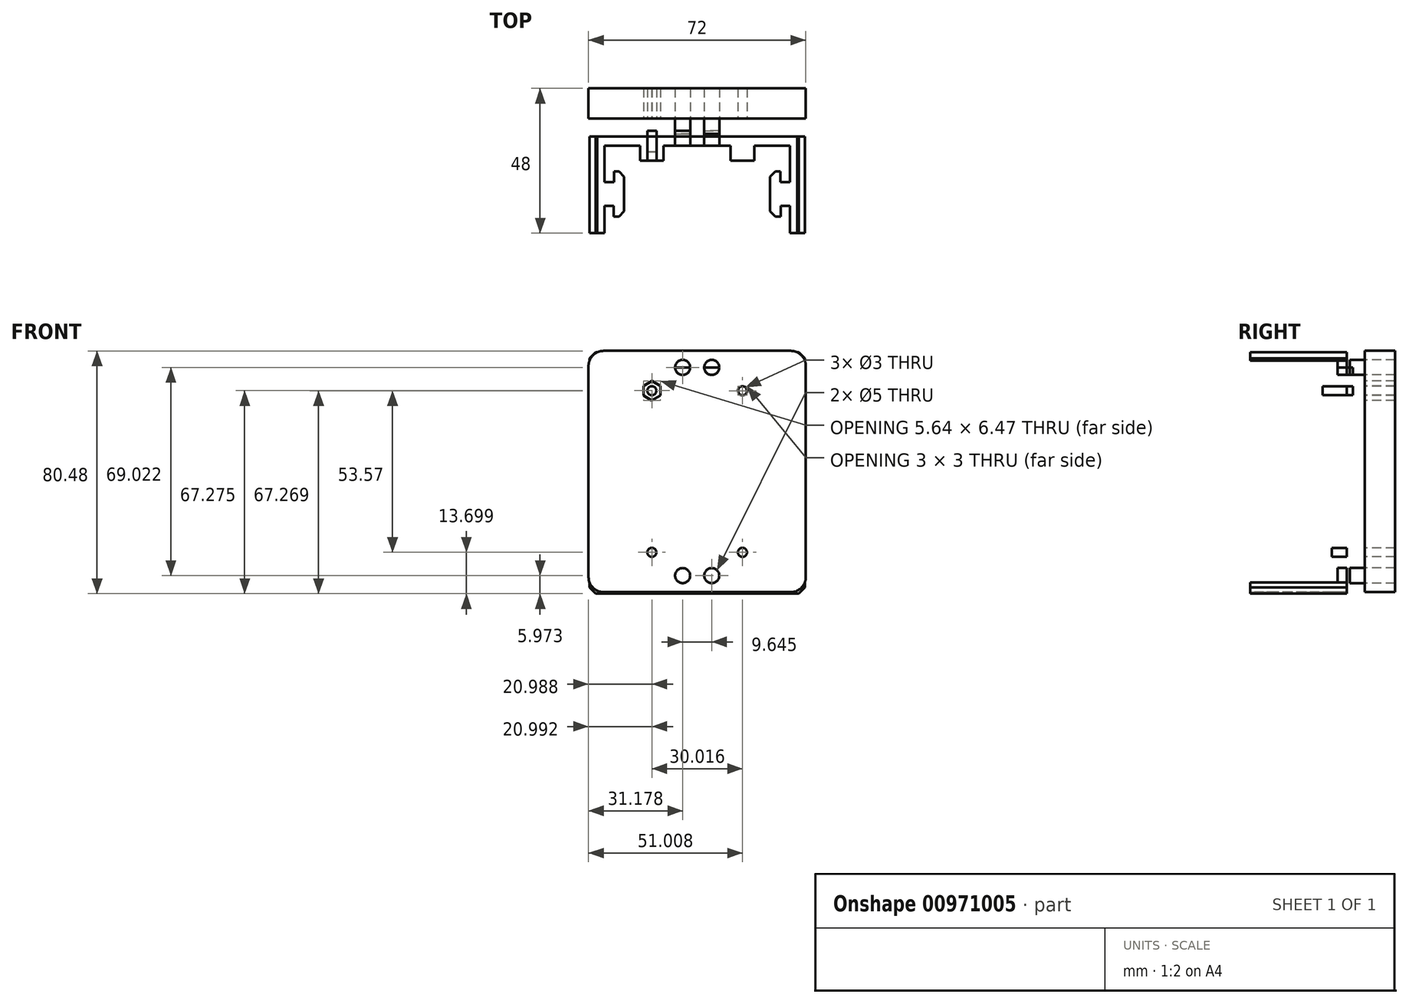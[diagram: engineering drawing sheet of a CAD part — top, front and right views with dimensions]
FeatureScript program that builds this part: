
annotation { "Feature Type Name" : "Feature", "Feature Type Description" : "" }
export const myFeature = defineFeature(function(context is Context, id is Id, definition is map)
    precondition{}
    {
        {
            var Q0;
            Q0=qCreatedBy(makeId("Top.planeOp"),FACE);
            var sketch = newSketch(context, id + "F0", { "sketchPlane" : qUnion([Q0])});
            skLineSegment(sketch, "E0.bottom", {"start": v(30, -15) * mm, "end": v(-30, -15) * mm});
            skLineSegment(sketch, "E0.top", {"start": v(30, 15) * mm, "end": v(-30, 15) * mm});
            skLineSegment(sketch, "E0.left", {"start": v(30, -15) * mm, "end": v(30, 15) * mm});
            skLineSegment(sketch, "E0.right", {"start": v(-30, -15) * mm, "end": v(-30, 15) * mm});
            skPoint(sketch, "E0.middle", {"position": v(0, 0) * mm});
            skLineSegment(sketch, "E1", {"start": v(0, 15) * mm, "end": v(0, -15) * mm});
            skLineSegment(sketch, "E2", {"start": v(35.69, 0) * mm, "end": v(35.69, 13) * mm});
            skLineSegment(sketch, "E3", {"start": v(35.69, 13) * mm, "end": v(35.69, 0) * mm});
            skLineSegment(sketch, "E4", {"start": v(35.69, -13) * mm, "end": v(35.69, 0) * mm});
            skLineSegment(sketch, "E5", {"start": v(35.69, 13) * mm, "end": v(30.75, 13) * mm});
            skLineSegment(sketch, "E6", {"start": v(30.75, 13) * mm, "end": v(30.75, -13) * mm});
            skLineSegment(sketch, "E7", {"start": v(30.75, -13) * mm, "end": v(35.69, -13) * mm});
            skLineSegment(sketch, "E8", {"start": v(35.69, 0) * mm, "end": v(24.19, 0) * mm});
            skLineSegment(sketch, "E9", {"start": v(24.19, 0) * mm, "end": v(24.19, -7.5) * mm});
            skLineSegment(sketch, "E10", {"start": v(24.19, -7.5) * mm, "end": v(24.19, 7.5) * mm});
            skLineSegment(sketch, "E11", {"start": v(24.19, 7.5) * mm, "end": v(27.59, 7.5) * mm});
            skLineSegment(sketch, "E12", {"start": v(27.59, 7.5) * mm, "end": v(27.59, 3.9) * mm});
            skLineSegment(sketch, "E13", {"start": v(27.59, 3.9) * mm, "end": v(30.75, 3.9) * mm});
            skLineSegment(sketch, "E14", {"start": v(30.75, 3.9) * mm, "end": v(30.75, -3.9) * mm});
            skLineSegment(sketch, "E15", {"start": v(30.75, -3.9) * mm, "end": v(27.65, -3.9) * mm});
            skLineSegment(sketch, "E16", {"start": v(27.65, -3.9) * mm, "end": v(27.65, -7.5) * mm});
            skLineSegment(sketch, "E17", {"start": v(27.65, -7.5) * mm, "end": v(24.19, -7.5) * mm});
            skLineSegment(sketch, "E18", {"start": v(25.89, 7.5) * mm, "end": v(24.19, 5.67) * mm});
            skLineSegment(sketch, "E19.MirrorCS", {"start": v(25.89, -7.5) * mm, "end": v(24.19, -5.67) * mm});
            skPoint(sketch, "E20.middle", {"position": v(33.19, 0) * mm});
            skLineSegment(sketch, "E21.bottom", {"start": v(30.75, 13) * mm, "end": v(35.69, 13) * mm});
            skLineSegment(sketch, "E21.left", {"start": v(30.75, 13) * mm, "end": v(30.75, 16) * mm});
            skLineSegment(sketch, "E21.right", {"start": v(35.69, 13) * mm, "end": v(35.69, 19) * mm});
            skLineSegment(sketch, "E22", {"start": v(15, 15) * mm, "end": v(15, -15) * mm, "construction": true});
            skLineSegment(sketch, "E23.bottom", {"start": v(18.9, 11) * mm, "end": v(11.1, 11) * mm});
            skLineSegment(sketch, "E23.top", {"start": v(18.9, 19) * mm, "end": v(11.1, 19) * mm});
            skLineSegment(sketch, "E23.left", {"start": v(18.9, 11) * mm, "end": v(18.9, 19) * mm});
            skLineSegment(sketch, "E23.right", {"start": v(11.1, 11) * mm, "end": v(11.1, 19) * mm});
            skPoint(sketch, "E23.middle", {"position": v(15, 15) * mm});
            skLineSegment(sketch, "E24", {"start": v(18.9, 19) * mm, "end": v(35.69, 19) * mm});
            skLineSegment(sketch, "E25", {"start": v(35.69, 19) * mm, "end": v(35.69, 19) * mm});
            skLineSegment(sketch, "E26", {"start": v(18.9, 16) * mm, "end": v(30.75, 16) * mm});
            skLineSegment(sketch, "E27", {"start": v(11.1, 19) * mm, "end": v(0, 19) * mm});
            skLineSegment(sketch, "E28", {"start": v(11.1, 16) * mm, "end": v(0, 16) * mm});
            skLineSegment(sketch, "E29", {"start": v(0, 16) * mm, "end": v(0, 19) * mm});
            skLineSegment(sketch, "E30.MirrorCS", {"start": v(-11.1, 16) * mm, "end": v(0, 16) * mm});
            skLineSegment(sketch, "E31.MirrorCS", {"start": v(-11.1, 11) * mm, "end": v(-11.1, 19) * mm});
            skLineSegment(sketch, "E32.MirrorCS", {"start": v(-18.9, 11) * mm, "end": v(-11.1, 11) * mm});
            skLineSegment(sketch, "E33.MirrorCS", {"start": v(-18.9, 11) * mm, "end": v(-18.9, 19) * mm});
            skLineSegment(sketch, "E34.MirrorCS", {"start": v(-18.9, 16) * mm, "end": v(-30.75, 16) * mm});
            skLineSegment(sketch, "E35.MirrorCS", {"start": v(-30.75, 13) * mm, "end": v(-30.75, 16) * mm});
            skLineSegment(sketch, "E36.MirrorCS", {"start": v(-35.69, 13) * mm, "end": v(-35.69, 19) * mm});
            skLineSegment(sketch, "E37.MirrorCS", {"start": v(-35.69, 19) * mm, "end": v(-35.69, 19) * mm});
            skLineSegment(sketch, "E38.MirrorCS", {"start": v(-18.9, 19) * mm, "end": v(-35.69, 19) * mm});
            skLineSegment(sketch, "E39.MirrorCS", {"start": v(-11.1, 19) * mm, "end": v(0, 19) * mm});
            skLineSegment(sketch, "E40.MirrorCS", {"start": v(-18.9, 19) * mm, "end": v(-11.1, 19) * mm});
            skLineSegment(sketch, "E41.MirrorCS", {"start": v(-30.75, 13) * mm, "end": v(-30.75, -13) * mm});
            skLineSegment(sketch, "E42.MirrorCS", {"start": v(-35.69, 13) * mm, "end": v(-35.69, 0) * mm});
            skLineSegment(sketch, "E43.MirrorCS", {"start": v(-30.75, -13) * mm, "end": v(-35.69, -13) * mm});
            skLineSegment(sketch, "E44.MirrorCS", {"start": v(-35.69, -13) * mm, "end": v(-35.69, 0) * mm});
            skLineSegment(sketch, "E45.MirrorCS", {"start": v(-30.75, -3.9) * mm, "end": v(-27.65, -3.9) * mm});
            skLineSegment(sketch, "E46.MirrorCS", {"start": v(-27.59, 3.9) * mm, "end": v(-30.75, 3.9) * mm});
            skLineSegment(sketch, "E47.MirrorCS", {"start": v(-24.19, -7.5) * mm, "end": v(-24.19, 7.5) * mm});
            skLineSegment(sketch, "E48.MirrorCS", {"start": v(-25.89, 7.5) * mm, "end": v(-24.19, 5.67) * mm});
            skLineSegment(sketch, "E49.MirrorCS", {"start": v(-24.19, 7.5) * mm, "end": v(-27.59, 7.5) * mm});
            skLineSegment(sketch, "E50.MirrorCS", {"start": v(-27.59, 7.5) * mm, "end": v(-27.59, 3.9) * mm});
            skLineSegment(sketch, "E51.MirrorCS", {"start": v(-27.65, -3.9) * mm, "end": v(-27.65, -7.5) * mm});
            skLineSegment(sketch, "E52.MirrorCS", {"start": v(-27.65, -7.5) * mm, "end": v(-24.19, -7.5) * mm});
            skLineSegment(sketch, "E53.MirrorCS", {"start": v(-25.89, -7.5) * mm, "end": v(-24.19, -5.67) * mm});
            skLineSegment(sketch, "E54.bottom", {"start": v(-35.69, 19) * mm, "end": v(35.69, 19) * mm});
            skLineSegment(sketch, "E54.top", {"start": v(-35.69, 21) * mm, "end": v(35.69, 21) * mm});
            skLineSegment(sketch, "E54.left", {"start": v(-35.69, 19) * mm, "end": v(-35.69, 21) * mm});
            skLineSegment(sketch, "E54.right", {"start": v(35.69, 19) * mm, "end": v(35.69, 21) * mm});
            skSolve(sketch);
        }
        {
            var Q0;
            {var subQ5=sQuery(id+"F0.wireOp",EDGE,"E4");Q0=makeQuery(id+"F0.imprint","IMPRINT",FACE,{"disambiguationData":[TD([[makeQuery(id+"F0.imprint","IMPRINT",EDGE,{"derivedFrom":subQ5}),1.0]])]});}
            var Q1;
            {var subQ3=sQuery(id+"F0.wireOp",EDGE,"E16");Q1=makeQuery(id+"F0.imprint","IMPRINT",FACE,{"disambiguationData":[TD([[makeQuery(id+"F0.imprint","IMPRINT",EDGE,{"derivedFrom":subQ3}),-1.0]])]});}
            var Q2;
            {var subQ0=sQuery(id+"F0.wireOp",EDGE,"E8");var subQ1=sQuery(id+"F0.wireOp",EDGE,"E0.left");var subQ2=makeQuery(id+"F0.imprint","INTERSECT",VERTEX,{"derivedFrom":[subQ1,subQ0]});Q2=makeQuery(id+"F0.imprint","IMPRINT",FACE,{"disambiguationData":[TD([[makeQuery(id+"F0.imprint","IMPRINT",EDGE,{"disambiguationData":[TD([[subQ2,1.0]])],"derivedFrom":subQ1}),-1.0]])]});}
            var Q3;
            {var subQ0=sQuery(id+"F0.wireOp",EDGE,"E13");var subQ1=sQuery(id+"F0.wireOp",EDGE,"E0.left");var subQ2=makeQuery(id+"F0.imprint","INTERSECT",VERTEX,{"derivedFrom":[subQ1,subQ0]});Q3=makeQuery(id+"F0.imprint","IMPRINT",FACE,{"disambiguationData":[TD([[makeQuery(id+"F0.imprint","IMPRINT",EDGE,{"disambiguationData":[TD([[subQ2,1.0]])],"derivedFrom":subQ1}),-1.0]])]});}
            var Q4;
            {var subQ7=sQuery(id+"F0.wireOp",EDGE,"E12");Q4=makeQuery(id+"F0.imprint","IMPRINT",FACE,{"disambiguationData":[TD([[makeQuery(id+"F0.imprint","IMPRINT",EDGE,{"derivedFrom":subQ7}),-1.0]])]});}
            var Q5;
            {var subQ5=sQuery(id+"F0.wireOp",EDGE,"E2");Q5=makeQuery(id+"F0.imprint","IMPRINT",FACE,{"disambiguationData":[TD([[makeQuery(id+"F0.imprint","IMPRINT",EDGE,{"derivedFrom":subQ5}),1.0]])]});}
            var Q6;
            Q6=makeQuery(id+"F0.imprint","IMPRINT",FACE,{"disambiguationData":[TD([[makeQuery(id+"F0.imprint","IMPRINT",EDGE,{"derivedFrom":sQuery(id+"F0.wireOp",EDGE,"E5")}),-1.0]])]});
            var Q7;
            {var subQ1=sQuery(id+"F0.wireOp",EDGE,"E23.top");Q7=makeQuery(id+"F0.imprint","IMPRINT",FACE,{"disambiguationData":[TD([[makeQuery(id+"F0.imprint","IMPRINT",EDGE,{"derivedFrom":subQ1}),1.0]])]});}
            var Q8;
            {var subQ0=sQuery(id+"F0.wireOp",EDGE,"E27");Q8=makeQuery(id+"F0.imprint","IMPRINT",FACE,{"disambiguationData":[TD([[makeQuery(id+"F0.imprint","IMPRINT",EDGE,{"derivedFrom":subQ0}),1.0]])]});}
            var Q9;
            Q9=makeQuery(id+"F0.imprint","IMPRINT",FACE,{"disambiguationData":[TD([[makeQuery(id+"F0.imprint","IMPRINT",EDGE,{"derivedFrom":sQuery(id+"F0.wireOp",EDGE,"E29")}),1.0]])]});
            var Q10;
            {var subQ6=sQuery(id+"F0.wireOp",EDGE,"E40.MirrorCS");Q10=makeQuery(id+"F0.imprint","IMPRINT",FACE,{"disambiguationData":[TD([[makeQuery(id+"F0.imprint","IMPRINT",EDGE,{"derivedFrom":subQ6}),-1.0]])]});}
            var Q11;
            {var subQ6=sQuery(id+"F0.wireOp",EDGE,"E34.MirrorCS");Q11=makeQuery(id+"F0.imprint","IMPRINT",FACE,{"disambiguationData":[TD([[makeQuery(id+"F0.imprint","IMPRINT",EDGE,{"derivedFrom":subQ6}),-1.0]])]});}
            var Q12;
            {var subQ5=sQuery(id+"F0.wireOp",EDGE,"E32.MirrorCS");Q12=makeQuery(id+"F0.imprint","IMPRINT",FACE,{"disambiguationData":[TD([[makeQuery(id+"F0.imprint","IMPRINT",EDGE,{"derivedFrom":subQ5}),1.0]])]});}
            var Q13;
            {var subQ5=sQuery(id+"F0.wireOp",EDGE,"E23.bottom");Q13=makeQuery(id+"F0.imprint","IMPRINT",FACE,{"disambiguationData":[TD([[makeQuery(id+"F0.imprint","IMPRINT",EDGE,{"derivedFrom":subQ5}),-1.0]])]});}
            var Q14;
            {var subQ2=sQuery(id+"F0.wireOp",EDGE,"E48.MirrorCS");Q14=makeQuery(id+"F0.imprint","IMPRINT",FACE,{"disambiguationData":[TD([[makeQuery(id+"F0.imprint","IMPRINT",EDGE,{"derivedFrom":subQ2}),-1.0]])]});}
            var Q15;
            {var subQ0=sQuery(id+"F0.wireOp",EDGE,"E46.MirrorCS");var subQ1=sQuery(id+"F0.wireOp",EDGE,"E0.right");var subQ2=makeQuery(id+"F0.imprint","INTERSECT",VERTEX,{"derivedFrom":[subQ1,subQ0]});Q15=makeQuery(id+"F0.imprint","IMPRINT",FACE,{"disambiguationData":[TD([[makeQuery(id+"F0.imprint","IMPRINT",EDGE,{"disambiguationData":[TD([[subQ2,1.0]])],"derivedFrom":subQ1}),1.0]])]});}
            var Q16;
            {var subQ2=sQuery(id+"F0.wireOp",EDGE,"E40.MirrorCS");Q16=makeQuery(id+"F0.imprint","IMPRINT",FACE,{"disambiguationData":[TD([[makeQuery(id+"F0.imprint","IMPRINT",EDGE,{"derivedFrom":subQ2}),-1.0]])]});}
            var Q17;
            Q17=makeQuery(id+"F0.imprint","IMPRINT",FACE,{"disambiguationData":[TD([[makeQuery(id+"F0.imprint","IMPRINT",EDGE,{"derivedFrom":sQuery(id+"F0.wireOp",EDGE,"E23.top")}),-1.0]])]});
            var Q18;
            {var subQ4=sQuery(id+"F0.wireOp",EDGE,"E23.top");Q18=makeQuery(id+"F0.imprint","IMPRINT",FACE,{"disambiguationData":[TD([[makeQuery(id+"F0.imprint","IMPRINT",EDGE,{"derivedFrom":subQ4}),1.0]])]});}
            var Q19;
            {var subQ0=sQuery(id+"F0.wireOp",EDGE,"E27");Q19=makeQuery(id+"F0.imprint","IMPRINT",FACE,{"disambiguationData":[TD([[makeQuery(id+"F0.imprint","IMPRINT",EDGE,{"derivedFrom":subQ0}),1.0]])]});}
            extrude(context, id + "F1", {"entities" : qUnion([Q0, Q1, Q2, Q3, Q4, Q5, Q6, Q7, Q8, Q9, Q10, Q11, Q12, Q13, Q14, Q15, Q16, Q17, Q18, Q19]), "oppositeDirection" : true, "depth" : 20 * mm, "offsetDistance" : 25 * mm});
        }
        {
            var Q0;
            Q0=makeQuery(id+"F1.opExtrude","SWEPT_FACE",FACE,{"disambiguationData":[OSD([sQuery(id+"F0.wireOp",EDGE,"E32.MirrorCS")])]});
            var Q1;
            Q1=makeQuery(id+"F1.opExtrude","SWEPT_FACE",FACE,{"disambiguationData":[OSD([sQuery(id+"F0.wireOp",EDGE,"E23.bottom")])]});
            var Q2;
            Q2=makeQuery(id+"F1.opExtrude","SWEPT_EDGE",EDGE,{"disambiguationData":[OSD([sQuery(id+"F0.wireOp",EDGE,"E43.MirrorCS"),sQuery(id+"F0.wireOp",EDGE,"E44.MirrorCS")])]});
            var Q3;
            Q3=makeQuery(id+"F1.opExtrude","SWEPT_EDGE",EDGE,{"disambiguationData":[OSD([sQuery(id+"F0.wireOp",EDGE,"E41.MirrorCS"),sQuery(id+"F0.wireOp",EDGE,"E43.MirrorCS")])]});
            var Q4;
            Q4=makeQuery(id+"F1.opExtrude","SWEPT_EDGE",EDGE,{"disambiguationData":[OSD([sQuery(id+"F0.wireOp",EDGE,"E6"),sQuery(id+"F0.wireOp",EDGE,"E7")])]});
            var Q5;
            Q5=makeQuery(id+"F1.opExtrude","SWEPT_EDGE",EDGE,{"disambiguationData":[OSD([sQuery(id+"F0.wireOp",EDGE,"E4"),sQuery(id+"F0.wireOp",EDGE,"E7")])]});
            var Q6;
            Q6=makeQuery(id+"F1.opExtrude","SWEPT_EDGE",EDGE,{"disambiguationData":[OSD([sQuery(id+"F0.wireOp",EDGE,"E24"),sQuery(id+"F0.wireOp",EDGE,"E25")])]});
            var Q7;
            Q7=makeQuery(id+"F1.opExtrude","SWEPT_EDGE",EDGE,{"disambiguationData":[OSD([sQuery(id+"F0.wireOp",EDGE,"E37.MirrorCS"),sQuery(id+"F0.wireOp",EDGE,"E38.MirrorCS")])]});
            chamfer(context, id + "F2", {"entities" : qUnion([Q0, Q1, Q2, Q3, Q4, Q5, Q6, Q7]), "width" : 1.2 * mm, "tangentPropagation" : true});
        }
        {
            var Q0;
            {var subQ6=sQuery(id+"F0.wireOp",EDGE,"E34.MirrorCS");Q0=makeQuery(id+"F0.imprint","IMPRINT",FACE,{"disambiguationData":[TD([[makeQuery(id+"F0.imprint","IMPRINT",EDGE,{"derivedFrom":subQ6}),-1.0]])]});}
            var Q1;
            {var subQ0=sQuery(id+"F0.wireOp",EDGE,"E46.MirrorCS");var subQ1=sQuery(id+"F0.wireOp",EDGE,"E0.right");var subQ2=makeQuery(id+"F0.imprint","INTERSECT",VERTEX,{"derivedFrom":[subQ1,subQ0]});Q1=makeQuery(id+"F0.imprint","IMPRINT",FACE,{"disambiguationData":[TD([[makeQuery(id+"F0.imprint","IMPRINT",EDGE,{"disambiguationData":[TD([[subQ2,1.0]])],"derivedFrom":subQ1}),1.0]])]});}
            var Q2;
            {var subQ2=sQuery(id+"F0.wireOp",EDGE,"E48.MirrorCS");Q2=makeQuery(id+"F0.imprint","IMPRINT",FACE,{"disambiguationData":[TD([[makeQuery(id+"F0.imprint","IMPRINT",EDGE,{"derivedFrom":subQ2}),-1.0]])]});}
            var Q3;
            {var subQ2=sQuery(id+"F0.wireOp",EDGE,"E40.MirrorCS");Q3=makeQuery(id+"F0.imprint","IMPRINT",FACE,{"disambiguationData":[TD([[makeQuery(id+"F0.imprint","IMPRINT",EDGE,{"derivedFrom":subQ2}),-1.0]])]});}
            var Q4;
            Q4=makeQuery(id+"F0.imprint","IMPRINT",FACE,{"disambiguationData":[TD([[makeQuery(id+"F0.imprint","IMPRINT",EDGE,{"derivedFrom":sQuery(id+"F0.wireOp",EDGE,"E29")}),1.0]])]});
            var Q5;
            {var subQ0=sQuery(id+"F0.wireOp",EDGE,"E27");Q5=makeQuery(id+"F0.imprint","IMPRINT",FACE,{"disambiguationData":[TD([[makeQuery(id+"F0.imprint","IMPRINT",EDGE,{"derivedFrom":subQ0}),1.0]])]});}
            var Q6;
            {var subQ4=sQuery(id+"F0.wireOp",EDGE,"E23.top");Q6=makeQuery(id+"F0.imprint","IMPRINT",FACE,{"disambiguationData":[TD([[makeQuery(id+"F0.imprint","IMPRINT",EDGE,{"derivedFrom":subQ4}),1.0]])]});}
            var Q7;
            Q7=makeQuery(id+"F0.imprint","IMPRINT",FACE,{"disambiguationData":[TD([[makeQuery(id+"F0.imprint","IMPRINT",EDGE,{"derivedFrom":sQuery(id+"F0.wireOp",EDGE,"E5")}),-1.0]])]});
            var Q8;
            {var subQ5=sQuery(id+"F0.wireOp",EDGE,"E2");Q8=makeQuery(id+"F0.imprint","IMPRINT",FACE,{"disambiguationData":[TD([[makeQuery(id+"F0.imprint","IMPRINT",EDGE,{"derivedFrom":subQ5}),1.0]])]});}
            var Q9;
            {var subQ5=sQuery(id+"F0.wireOp",EDGE,"E4");Q9=makeQuery(id+"F0.imprint","IMPRINT",FACE,{"disambiguationData":[TD([[makeQuery(id+"F0.imprint","IMPRINT",EDGE,{"derivedFrom":subQ5}),1.0]])]});}
            var Q10;
            {var subQ3=sQuery(id+"F0.wireOp",EDGE,"E16");Q10=makeQuery(id+"F0.imprint","IMPRINT",FACE,{"disambiguationData":[TD([[makeQuery(id+"F0.imprint","IMPRINT",EDGE,{"derivedFrom":subQ3}),-1.0]])]});}
            var Q11;
            Q11=makeQuery(id+"F0.imprint","IMPRINT",FACE,{"disambiguationData":[TD([[makeQuery(id+"F0.imprint","IMPRINT",EDGE,{"derivedFrom":sQuery(id+"F0.wireOp",EDGE,"E23.top")}),-1.0]])]});
            var Q12;
            {var subQ5=sQuery(id+"F0.wireOp",EDGE,"E32.MirrorCS");Q12=makeQuery(id+"F0.imprint","IMPRINT",FACE,{"disambiguationData":[TD([[makeQuery(id+"F0.imprint","IMPRINT",EDGE,{"derivedFrom":subQ5}),1.0]])]});}
            var Q13;
            {var subQ5=sQuery(id+"F0.wireOp",EDGE,"E23.bottom");Q13=makeQuery(id+"F0.imprint","IMPRINT",FACE,{"disambiguationData":[TD([[makeQuery(id+"F0.imprint","IMPRINT",EDGE,{"derivedFrom":subQ5}),-1.0]])]});}
            var Q14;
            {var subQ7=sQuery(id+"F0.wireOp",EDGE,"E12");Q14=makeQuery(id+"F0.imprint","IMPRINT",FACE,{"disambiguationData":[TD([[makeQuery(id+"F0.imprint","IMPRINT",EDGE,{"derivedFrom":subQ7}),-1.0]])]});}
            var Q15;
            {var subQ0=sQuery(id+"F0.wireOp",EDGE,"E8");var subQ1=sQuery(id+"F0.wireOp",EDGE,"E0.left");var subQ2=makeQuery(id+"F0.imprint","INTERSECT",VERTEX,{"derivedFrom":[subQ1,subQ0]});Q15=makeQuery(id+"F0.imprint","IMPRINT",FACE,{"disambiguationData":[TD([[makeQuery(id+"F0.imprint","IMPRINT",EDGE,{"disambiguationData":[TD([[subQ2,1.0]])],"derivedFrom":subQ1}),-1.0]])]});}
            var Q16;
            {var subQ0=sQuery(id+"F0.wireOp",EDGE,"E13");var subQ1=sQuery(id+"F0.wireOp",EDGE,"E0.left");var subQ2=makeQuery(id+"F0.imprint","INTERSECT",VERTEX,{"derivedFrom":[subQ1,subQ0]});Q16=makeQuery(id+"F0.imprint","IMPRINT",FACE,{"disambiguationData":[TD([[makeQuery(id+"F0.imprint","IMPRINT",EDGE,{"disambiguationData":[TD([[subQ2,1.0]])],"derivedFrom":subQ1}),-1.0]])]});}
            extrude(context, id + "F3", {"entities" : qUnion([Q0, Q1, Q2, Q3, Q4, Q5, Q6, Q7, Q8, Q9, Q10, Q11, Q12, Q13, Q14, Q15, Q16]), "depth" : 15 * mm, "offsetDistance" : 25 * mm});
        }
        {
            var Q0;
            Q0=makeQuery(id+"F3.opExtrude","SWEPT_EDGE",EDGE,{"disambiguationData":[OSD([sQuery(id+"F0.wireOp",EDGE,"E41.MirrorCS"),sQuery(id+"F0.wireOp",EDGE,"E43.MirrorCS")])]});
            var Q1;
            Q1=makeQuery(id+"F3.opExtrude","SWEPT_EDGE",EDGE,{"disambiguationData":[OSD([sQuery(id+"F0.wireOp",EDGE,"E43.MirrorCS"),sQuery(id+"F0.wireOp",EDGE,"E44.MirrorCS")])]});
            var Q2;
            Q2=makeQuery(id+"F3.opExtrude","SWEPT_EDGE",EDGE,{"disambiguationData":[OSD([sQuery(id+"F0.wireOp",EDGE,"E6"),sQuery(id+"F0.wireOp",EDGE,"E7")])]});
            var Q3;
            Q3=makeQuery(id+"F3.opExtrude","SWEPT_EDGE",EDGE,{"disambiguationData":[OSD([sQuery(id+"F0.wireOp",EDGE,"E4"),sQuery(id+"F0.wireOp",EDGE,"E7")])]});
            var Q4;
            Q4=makeQuery(id+"F3.opExtrude","SWEPT_FACE",FACE,{"disambiguationData":[OSD([sQuery(id+"F0.wireOp",EDGE,"E23.bottom")])]});
            var Q5;
            Q5=makeQuery(id+"F3.opExtrude","SWEPT_FACE",FACE,{"disambiguationData":[OSD([sQuery(id+"F0.wireOp",EDGE,"E32.MirrorCS")])]});
            chamfer(context, id + "F4", {"entities" : qUnion([Q0, Q1, Q2, Q3, Q4, Q5]), "width" : 1 * mm, "tangentPropagation" : true});
        }
        {
            var Q0;
            Q0=qCreatedBy(makeId("Front.planeOp"),FACE);
            var sketch = newSketch(context, id + "F5", { "sketchPlane" : qUnion([Q0])});
            skLineSegment(sketch, "E55.bottom", {"start": v(-31, -59.52) * mm, "end": v(31, -59.52) * mm});
            skLineSegment(sketch, "E55.top", {"start": v(-31, 20.48) * mm, "end": v(31, 20.48) * mm});
            skLineSegment(sketch, "E55.left", {"start": v(-36, -54.52) * mm, "end": v(-36, 15.48) * mm});
            skLineSegment(sketch, "E55.right", {"start": v(36, -54.52) * mm, "end": v(36, 15.48) * mm});
            skPoint(sketch, "E55.middle", {"position": v(0, 0) * mm});
            skCircle(sketch, "E56", {"center": v(-15, 7.27) * mm, "radius": 1.5 * mm});
            skCircle(sketch, "E57.MirrorC", {"center": v(15, 7.27) * mm, "radius": 1.5 * mm});
            skPoint(sketch, "E58.visualSharp", {"position": v(36, 20.48) * mm});
            skArc(sketch, "E58.filletArc", {"start": v(36, 15.48) * mm, "mid": v(34.54, 19.02) * mm, "end": v(31, 20.48) * mm});
            skPoint(sketch, "E59.visualSharp", {"position": v(-36, 20.48) * mm});
            skArc(sketch, "E59.filletArc", {"start": v(-31, 20.48) * mm, "mid": v(-34.54, 19.02) * mm, "end": v(-36, 15.48) * mm});
            skPoint(sketch, "E60.visualSharp", {"position": v(-36, -59.52) * mm});
            skArc(sketch, "E60.filletArc", {"start": v(-36, -54.52) * mm, "mid": v(-34.54, -58.05) * mm, "end": v(-31, -59.52) * mm});
            skPoint(sketch, "E61.visualSharp", {"position": v(36, -59.52) * mm});
            skArc(sketch, "E61.filletArc", {"start": v(31, -59.52) * mm, "mid": v(34.54, -58.05) * mm, "end": v(36, -54.52) * mm});
            skLineSegment(sketch, "E62", {"start": v(36, -19.52) * mm, "end": v(-36, -19.52) * mm, "construction": true});
            skCircle(sketch, "E63.MirrorC", {"center": v(-15, -46.3) * mm, "radius": 1.5 * mm});
            skCircle(sketch, "E64.MirrorC", {"center": v(15, -46.3) * mm, "radius": 1.5 * mm});
            skCircle(sketch, "E65", {"center": v(4.82, 15) * mm, "radius": 2.5 * mm});
            skCircle(sketch, "E66.MirrorC", {"center": v(-4.82, 15) * mm, "radius": 2.5 * mm});
            skCircle(sketch, "E67.MirrorC", {"center": v(4.82, -54.03) * mm, "radius": 2.5 * mm});
            skCircle(sketch, "E68.MirrorC", {"center": v(-4.82, -54.03) * mm, "radius": 2.5 * mm});
            skSolve(sketch);
        }
        {
            var Q0;
            Q0=makeQuery(id+"F3.opExtrude","SWEPT_FACE",FACE,{"disambiguationData":[OSD([sQuery(id+"F0.wireOp",EDGE,"E23.bottom")])]});
            var sketch = newSketch(context, id + "F6", { "sketchPlane" : qUnion([Q0])});
            skCircle(sketch, "E69", {"center": v(15.01, 7.28) * mm, "radius": 1.5 * mm});
            skCircle(sketch, "E70.cCircle", {"center": v(15.01, 7.28) * mm, "radius": 2.8 * mm, "construction": true});
            skLineSegment(sketch, "E70.0", {"start": v(12.2, 8.86) * mm, "end": v(14.98, 10.5) * mm});
            skLineSegment(sketch, "E70.1", {"start": v(14.98, 10.5) * mm, "end": v(17.8, 8.92) * mm});
            skLineSegment(sketch, "E70.2", {"start": v(17.8, 8.92) * mm, "end": v(17.83, 5.7) * mm});
            skLineSegment(sketch, "E70.3", {"start": v(17.83, 5.7) * mm, "end": v(15.05, 4.04) * mm});
            skLineSegment(sketch, "E70.4", {"start": v(15.05, 4.04) * mm, "end": v(12.23, 5.63) * mm});
            skLineSegment(sketch, "E70.5", {"start": v(12.23, 5.63) * mm, "end": v(12.2, 8.86) * mm});
            skPoint(sketch, "E70.0.midPoint", {"position": v(13.58, 9.68) * mm});
            skLineSegment(sketch, "E71.MirrorCS", {"start": v(-15.05, 4.04) * mm, "end": v(-12.23, 5.63) * mm});
            skLineSegment(sketch, "E72.MirrorCS", {"start": v(-12.23, 5.63) * mm, "end": v(-12.2, 8.86) * mm});
            skLineSegment(sketch, "E73.MirrorCS", {"start": v(-12.2, 8.86) * mm, "end": v(-14.98, 10.5) * mm});
            skLineSegment(sketch, "E74.MirrorCS", {"start": v(-14.98, 10.5) * mm, "end": v(-17.8, 8.92) * mm});
            skLineSegment(sketch, "E75.MirrorCS", {"start": v(-17.8, 8.92) * mm, "end": v(-17.83, 5.7) * mm});
            skLineSegment(sketch, "E76.MirrorCS", {"start": v(-17.83, 5.7) * mm, "end": v(-15.05, 4.04) * mm});
            skCircle(sketch, "E77.MirrorC", {"center": v(-15.01, 7.28) * mm, "radius": 1.5 * mm});
            skCircle(sketch, "E78.cCircle", {"center": v(-14.94, -46.17) * mm, "radius": 2.8 * mm, "construction": true});
            skLineSegment(sketch, "E78.0", {"start": v(-14.9, -49.4) * mm, "end": v(-17.72, -47.83) * mm});
            skLineSegment(sketch, "E78.1", {"start": v(-17.72, -47.83) * mm, "end": v(-17.76, -44.6) * mm});
            skLineSegment(sketch, "E78.2", {"start": v(-17.76, -44.6) * mm, "end": v(-14.99, -42.94) * mm});
            skLineSegment(sketch, "E78.3", {"start": v(-14.99, -42.94) * mm, "end": v(-12.16, -44.52) * mm});
            skLineSegment(sketch, "E78.4", {"start": v(-12.16, -44.52) * mm, "end": v(-12.12, -47.75) * mm});
            skLineSegment(sketch, "E78.5", {"start": v(-12.12, -47.75) * mm, "end": v(-14.9, -49.4) * mm});
            skPoint(sketch, "E78.0.midPoint", {"position": v(-16.3, -48.61) * mm});
            skLineSegment(sketch, "E79.MirrorCS", {"start": v(17.72, -47.83) * mm, "end": v(17.76, -44.6) * mm});
            skLineSegment(sketch, "E80.MirrorCS", {"start": v(17.76, -44.6) * mm, "end": v(14.99, -42.94) * mm});
            skLineSegment(sketch, "E81.MirrorCS", {"start": v(14.9, -49.4) * mm, "end": v(17.72, -47.83) * mm});
            skLineSegment(sketch, "E82.MirrorCS", {"start": v(12.16, -44.52) * mm, "end": v(12.12, -47.75) * mm});
            skLineSegment(sketch, "E83.MirrorCS", {"start": v(12.12, -47.75) * mm, "end": v(14.9, -49.4) * mm});
            skLineSegment(sketch, "E84.MirrorCS", {"start": v(14.99, -42.94) * mm, "end": v(12.16, -44.52) * mm});
            skPoint(sketch, "E85.MirrorP", {"position": v(16.3, -48.61) * mm});
            skCircle(sketch, "E86.MirrorC", {"center": v(14.94, -46.17) * mm, "radius": 2.8 * mm, "construction": true});
            skSolve(sketch);
        }
        {
            var Q0;
            Q0 = qSketchRegion(id + "F5", true);
            var Q1;
            Q1=makeQuery(id+"F5.imprint","IMPRINT",FACE,{"disambiguationData":[TD([[makeQuery(id+"F5.imprint","IMPRINT",EDGE,{"derivedFrom":sQuery(id+"F5.wireOp",EDGE,"E65")}),1.0]])]});
            var Q2;
            Q2=makeQuery(id+"F5.imprint","IMPRINT",FACE,{"disambiguationData":[TD([[makeQuery(id+"F5.imprint","IMPRINT",EDGE,{"derivedFrom":sQuery(id+"F5.wireOp",EDGE,"E66.MirrorC")}),-1.0]])]});
            var Q3;
            Q3=makeQuery(id+"F5.imprint","IMPRINT",FACE,{"disambiguationData":[TD([[makeQuery(id+"F5.imprint","IMPRINT",EDGE,{"derivedFrom":sQuery(id+"F5.wireOp",EDGE,"E67.MirrorC")}),-1.0]])]});
            var Q4;
            Q4=makeQuery(id+"F5.imprint","IMPRINT",FACE,{"disambiguationData":[TD([[makeQuery(id+"F5.imprint","IMPRINT",EDGE,{"derivedFrom":sQuery(id+"F5.wireOp",EDGE,"E68.MirrorC")}),1.0]])]});
            extrude(context, id + "F7", {"entities" : qUnion([Q0, Q1, Q2, Q3, Q4]), "oppositeDirection" : true, "depth" : 25 * mm, "offsetDistance" : 25 * mm, "hasSecondDirection" : true, "secondDirectionOppositeDirection" : true, "secondDirectionDepth" : 20 * mm});
        }
        {
            var Q0;
            Q0=makeQuery(id+"F5.imprint","IMPRINT",FACE,{"disambiguationData":[TD([[makeQuery(id+"F5.imprint","IMPRINT",EDGE,{"derivedFrom":sQuery(id+"F5.wireOp",EDGE,"E65")}),1.0]])]});
            var Q1;
            Q1=makeQuery(id+"F5.imprint","IMPRINT",FACE,{"disambiguationData":[TD([[makeQuery(id+"F5.imprint","IMPRINT",EDGE,{"derivedFrom":sQuery(id+"F5.wireOp",EDGE,"E66.MirrorC")}),-1.0]])]});
            var Q2;
            Q2=makeQuery(id+"F5.imprint","IMPRINT",FACE,{"disambiguationData":[TD([[makeQuery(id+"F5.imprint","IMPRINT",EDGE,{"derivedFrom":sQuery(id+"F5.wireOp",EDGE,"E68.MirrorC")}),1.0]])]});
            var Q3;
            Q3=makeQuery(id+"F5.imprint","IMPRINT",FACE,{"disambiguationData":[TD([[makeQuery(id+"F5.imprint","IMPRINT",EDGE,{"derivedFrom":sQuery(id+"F5.wireOp",EDGE,"E67.MirrorC")}),-1.0]])]});
            extrude(context, id + "F8", {"entities" : qUnion([Q0, Q1, Q2, Q3]), "operationType" : NewBodyOperationType.ADD, "oppositeDirection" : true, "depth" : 35 * mm, "offsetDistance" : 25 * mm, "hasSecondDirection" : true, "secondDirectionOppositeDirection" : true, "secondDirectionDepth" : 25 * mm});
        }
        {
            var Q0;
            {var subQ2=sQuery(id+"F0.wireOp",EDGE,"E48.MirrorCS");Q0=makeQuery(id+"F0.imprint","IMPRINT",FACE,{"disambiguationData":[TD([[makeQuery(id+"F0.imprint","IMPRINT",EDGE,{"derivedFrom":subQ2}),-1.0]])]});}
            var Q1;
            {var subQ0=sQuery(id+"F0.wireOp",EDGE,"E46.MirrorCS");var subQ1=sQuery(id+"F0.wireOp",EDGE,"E0.right");var subQ2=makeQuery(id+"F0.imprint","INTERSECT",VERTEX,{"derivedFrom":[subQ1,subQ0]});Q1=makeQuery(id+"F0.imprint","IMPRINT",FACE,{"disambiguationData":[TD([[makeQuery(id+"F0.imprint","IMPRINT",EDGE,{"disambiguationData":[TD([[subQ2,1.0]])],"derivedFrom":subQ1}),1.0]])]});}
            var Q2;
            {var subQ6=sQuery(id+"F0.wireOp",EDGE,"E34.MirrorCS");Q2=makeQuery(id+"F0.imprint","IMPRINT",FACE,{"disambiguationData":[TD([[makeQuery(id+"F0.imprint","IMPRINT",EDGE,{"derivedFrom":subQ6}),-1.0]])]});}
            var Q3;
            {var subQ5=sQuery(id+"F0.wireOp",EDGE,"E32.MirrorCS");Q3=makeQuery(id+"F0.imprint","IMPRINT",FACE,{"disambiguationData":[TD([[makeQuery(id+"F0.imprint","IMPRINT",EDGE,{"derivedFrom":subQ5}),1.0]])]});}
            var Q4;
            {var subQ2=sQuery(id+"F0.wireOp",EDGE,"E40.MirrorCS");Q4=makeQuery(id+"F0.imprint","IMPRINT",FACE,{"disambiguationData":[TD([[makeQuery(id+"F0.imprint","IMPRINT",EDGE,{"derivedFrom":subQ2}),-1.0]])]});}
            var Q5;
            Q5=makeQuery(id+"F0.imprint","IMPRINT",FACE,{"disambiguationData":[TD([[makeQuery(id+"F0.imprint","IMPRINT",EDGE,{"derivedFrom":sQuery(id+"F0.wireOp",EDGE,"E29")}),1.0]])]});
            var Q6;
            {var subQ0=sQuery(id+"F0.wireOp",EDGE,"E27");Q6=makeQuery(id+"F0.imprint","IMPRINT",FACE,{"disambiguationData":[TD([[makeQuery(id+"F0.imprint","IMPRINT",EDGE,{"derivedFrom":subQ0}),1.0]])]});}
            var Q7;
            {var subQ5=sQuery(id+"F0.wireOp",EDGE,"E23.bottom");Q7=makeQuery(id+"F0.imprint","IMPRINT",FACE,{"disambiguationData":[TD([[makeQuery(id+"F0.imprint","IMPRINT",EDGE,{"derivedFrom":subQ5}),-1.0]])]});}
            var Q8;
            {var subQ5=sQuery(id+"F0.wireOp",EDGE,"E2");Q8=makeQuery(id+"F0.imprint","IMPRINT",FACE,{"disambiguationData":[TD([[makeQuery(id+"F0.imprint","IMPRINT",EDGE,{"derivedFrom":subQ5}),1.0]])]});}
            var Q9;
            Q9=makeQuery(id+"F0.imprint","IMPRINT",FACE,{"disambiguationData":[TD([[makeQuery(id+"F0.imprint","IMPRINT",EDGE,{"derivedFrom":sQuery(id+"F0.wireOp",EDGE,"E5")}),-1.0]])]});
            var Q10;
            {var subQ4=sQuery(id+"F0.wireOp",EDGE,"E23.top");Q10=makeQuery(id+"F0.imprint","IMPRINT",FACE,{"disambiguationData":[TD([[makeQuery(id+"F0.imprint","IMPRINT",EDGE,{"derivedFrom":subQ4}),1.0]])]});}
            var Q11;
            {var subQ7=sQuery(id+"F0.wireOp",EDGE,"E12");Q11=makeQuery(id+"F0.imprint","IMPRINT",FACE,{"disambiguationData":[TD([[makeQuery(id+"F0.imprint","IMPRINT",EDGE,{"derivedFrom":subQ7}),-1.0]])]});}
            var Q12;
            {var subQ0=sQuery(id+"F0.wireOp",EDGE,"E13");var subQ1=sQuery(id+"F0.wireOp",EDGE,"E0.left");var subQ2=makeQuery(id+"F0.imprint","INTERSECT",VERTEX,{"derivedFrom":[subQ1,subQ0]});Q12=makeQuery(id+"F0.imprint","IMPRINT",FACE,{"disambiguationData":[TD([[makeQuery(id+"F0.imprint","IMPRINT",EDGE,{"disambiguationData":[TD([[subQ2,1.0]])],"derivedFrom":subQ1}),-1.0]])]});}
            var Q13;
            {var subQ0=sQuery(id+"F0.wireOp",EDGE,"E8");var subQ1=sQuery(id+"F0.wireOp",EDGE,"E0.left");var subQ2=makeQuery(id+"F0.imprint","INTERSECT",VERTEX,{"derivedFrom":[subQ1,subQ0]});Q13=makeQuery(id+"F0.imprint","IMPRINT",FACE,{"disambiguationData":[TD([[makeQuery(id+"F0.imprint","IMPRINT",EDGE,{"disambiguationData":[TD([[subQ2,1.0]])],"derivedFrom":subQ1}),-1.0]])]});}
            var Q14;
            {var subQ3=sQuery(id+"F0.wireOp",EDGE,"E16");Q14=makeQuery(id+"F0.imprint","IMPRINT",FACE,{"disambiguationData":[TD([[makeQuery(id+"F0.imprint","IMPRINT",EDGE,{"derivedFrom":subQ3}),-1.0]])]});}
            var Q15;
            {var subQ5=sQuery(id+"F0.wireOp",EDGE,"E4");Q15=makeQuery(id+"F0.imprint","IMPRINT",FACE,{"disambiguationData":[TD([[makeQuery(id+"F0.imprint","IMPRINT",EDGE,{"derivedFrom":subQ5}),1.0]])]});}
            extrude(context, id + "F9", {"entities" : qUnion([Q0, Q1, Q2, Q3, Q4, Q5, Q6, Q7, Q8, Q9, Q10, Q11, Q12, Q13, Q14, Q15]), "depth" : 20 * mm, "offsetDistance" : 25 * mm, "hasSecondDirection" : true, "secondDirectionOppositeDirection" : true, "secondDirectionDepth" : 60 * mm});
        }
        {
            var Q0;
            Q0=makeQuery(id+"F6.imprint","IMPRINT",FACE,{"disambiguationData":[TD([[makeQuery(id+"F6.imprint","IMPRINT",EDGE,{"derivedFrom":sQuery(id+"F6.wireOp",EDGE,"E69")}),1.0]])]});
            var Q1;
            {var subQ0=sQuery(id+"F6.wireOp",EDGE,"a8a6771a-7732-4efc-b70e-3c45288168380.MirrorC");var subQ1=sQuery(id+"F6.wireOp",EDGE,"rF9vHSOL-jpUe-XAlv-izzy-5frkWew4ku90");var subQ2=makeQuery(id+"F6.imprint","INTERSECT",VERTEX,{"disambiguationData":[OD(0.0)],"derivedFrom":[subQ1,subQ0]});Q1=makeQuery(id+"F6.imprint","IMPRINT",FACE,{"disambiguationData":[TD([[makeQuery(id+"F6.imprint","IMPRINT",EDGE,{"disambiguationData":[TD([[subQ2,-1.0]])],"derivedFrom":subQ1}),1.0]])]});}
            var Q2;
            Q2=makeQuery(id+"F6.imprint","IMPRINT",FACE,{"disambiguationData":[TD([[makeQuery(id+"F6.imprint","IMPRINT",EDGE,{"derivedFrom":sQuery(id+"F6.wireOp",EDGE,"E77.MirrorC")}),-1.0]])]});
            var Q3;
            Q3=makeQuery(id+"F5.imprint","IMPRINT",FACE,{"disambiguationData":[TD([[makeQuery(id+"F5.imprint","IMPRINT",EDGE,{"derivedFrom":sQuery(id+"F5.wireOp",EDGE,"E63.MirrorC")}),-1.0]])]});
            var Q4;
            Q4=makeQuery(id+"F5.imprint","IMPRINT",FACE,{"disambiguationData":[TD([[makeQuery(id+"F5.imprint","IMPRINT",EDGE,{"derivedFrom":sQuery(id+"F5.wireOp",EDGE,"E64.MirrorC")}),1.0]])]});
            extrude(context, id + "F10", {"entities" : qUnion([Q0, Q1, Q2, Q3, Q4]), "operationType" : NewBodyOperationType.REMOVE, "oppositeDirection" : true, "depth" : 25 * mm, "offsetDistance" : 25 * mm, "hasSecondDirection" : true, "secondDirectionOppositeDirection" : false, "secondDirectionDepth" : 25 * mm});
        }
        {
            var Q0;
            Q0 = qSketchRegion(id + "F6", true);
            extrude(context, id + "F11", {"entities" : qUnion([Q0]), "operationType" : NewBodyOperationType.REMOVE, "oppositeDirection" : true, "depth" : 3 * mm, "offsetDistance" : 25 * mm});
        }
        {
            var Q0;
            Q0=makeQuery(id+"F9.opExtrude","CAP_EDGE",EDGE,{"disambiguationData":[OSD([sQuery(id+"F0.wireOp",EDGE,"E36.MirrorCS"),sQuery(id+"F0.wireOp",EDGE,"E42.MirrorCS"),sQuery(id+"F0.wireOp",EDGE,"E44.MirrorCS")])],"isStart":false});
            var Q1;
            Q1=makeQuery(id+"F9.opExtrude","CAP_EDGE",EDGE,{"disambiguationData":[OSD([sQuery(id+"F0.wireOp",EDGE,"E2"),sQuery(id+"F0.wireOp",EDGE,"E4"),sQuery(id+"F0.wireOp",EDGE,"E21.right")])],"isStart":false});
            var Q2;
            Q2=makeQuery(id+"F9.opExtrude","CAP_EDGE",EDGE,{"disambiguationData":[OSD([sQuery(id+"F0.wireOp",EDGE,"E36.MirrorCS"),sQuery(id+"F0.wireOp",EDGE,"E42.MirrorCS"),sQuery(id+"F0.wireOp",EDGE,"E44.MirrorCS")])],"isStart":true});
            var Q3;
            Q3=makeQuery(id+"F9.opExtrude","CAP_EDGE",EDGE,{"disambiguationData":[OSD([sQuery(id+"F0.wireOp",EDGE,"E2"),sQuery(id+"F0.wireOp",EDGE,"E4"),sQuery(id+"F0.wireOp",EDGE,"E21.right")])],"isStart":true});
            chamfer(context, id + "F12", {"entities" : qUnion([Q0, Q1, Q2, Q3]), "width" : 2 * mm, "tangentPropagation" : true});
        }
    });
